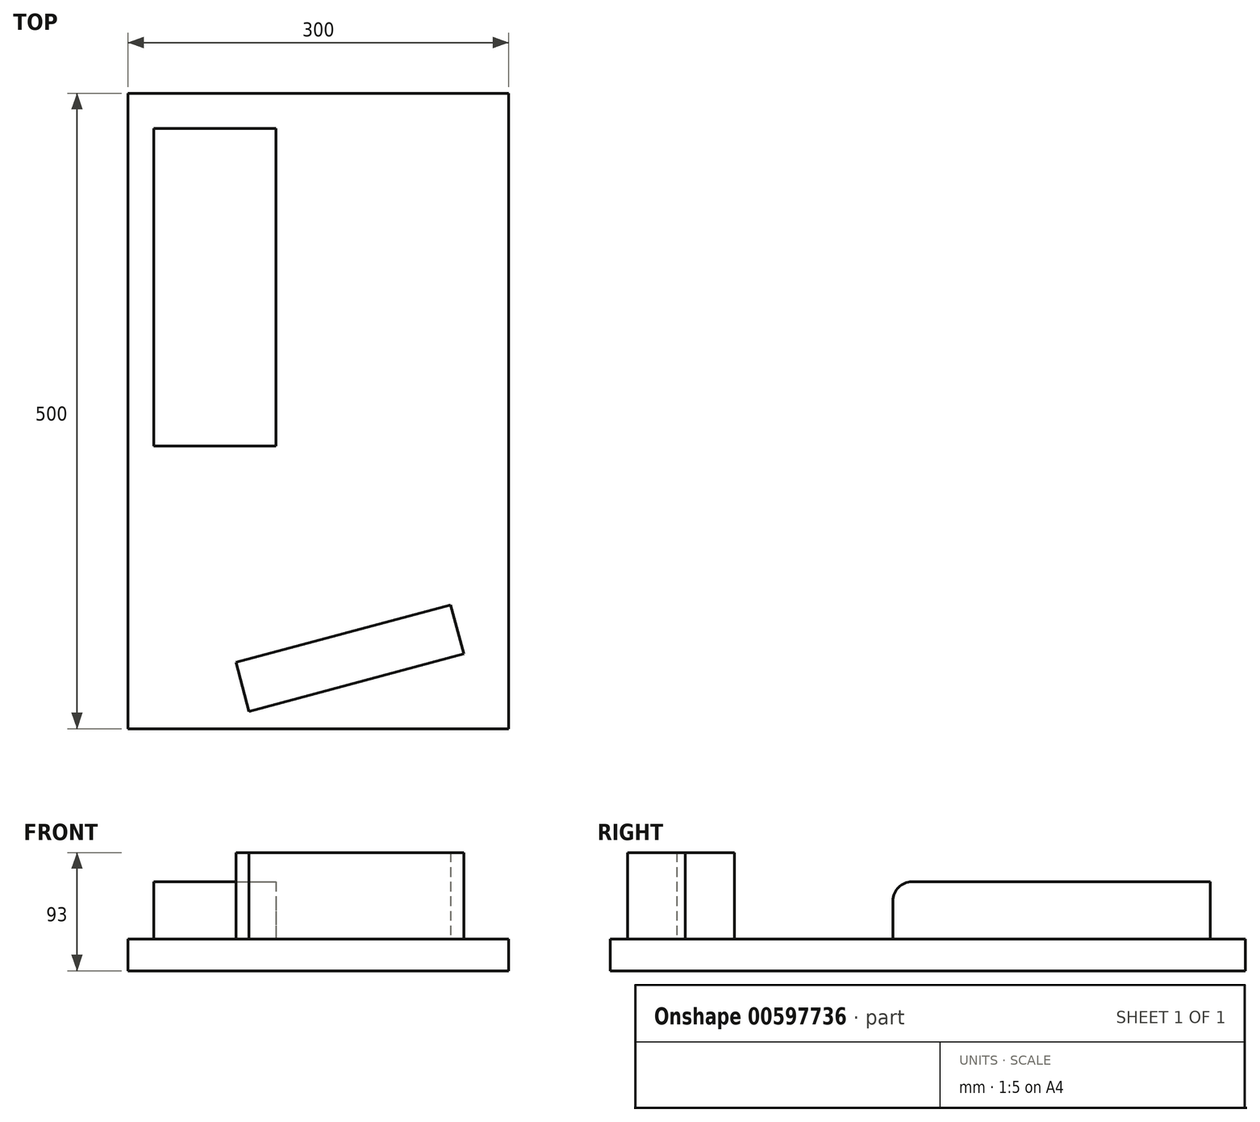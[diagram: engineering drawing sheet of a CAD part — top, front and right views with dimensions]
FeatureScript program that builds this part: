
annotation { "Feature Type Name" : "Feature", "Feature Type Description" : "" }
export const myFeature = defineFeature(function(context is Context, id is Id, definition is map)
    precondition{}
    {
        {
            var Q0;
            Q0=qCreatedBy(makeId("Top.planeOp"),FACE);
            var sketch = newSketch(context, id + "F0", { "sketchPlane" : qUnion([Q0])});
            skLineSegment(sketch, "E0.bottom", {"start": v(-250.75, 264.87) * mm, "end": v(49.25, 264.87) * mm});
            skLineSegment(sketch, "E0.top", {"start": v(-250.75, -235.13) * mm, "end": v(49.25, -235.13) * mm});
            skLineSegment(sketch, "E0.left", {"start": v(-250.75, 264.87) * mm, "end": v(-250.75, -235.13) * mm});
            skLineSegment(sketch, "E0.right", {"start": v(49.25, 264.87) * mm, "end": v(49.25, -235.13) * mm});
            skSolve(sketch);
        }
        {
            var Q0;
            Q0 = qSketchRegion(id + "F0", true);
            extrude(context, id + "F1", {"entities" : qUnion([Q0]), "depth" : 25 * mm, "offsetDistance" : 25 * mm});
        }
        {
            var Q0;
            Q0=makeQuery(id+"F1.opExtrude","CAP_FACE",FACE,{"disambiguationData":[OSD([sQuery(id+"F0.wireOp",EDGE,"E0.bottom"),sQuery(id+"F0.wireOp",EDGE,"E0.top"),sQuery(id+"F0.wireOp",EDGE,"E0.left"),sQuery(id+"F0.wireOp",EDGE,"E0.right")])],"isStart":false});
            var sketch = newSketch(context, id + "F2", { "sketchPlane" : qUnion([Q0])});
            skLineSegment(sketch, "E1.bottom", {"start": v(-230.17, 237.28) * mm, "end": v(-134.17, 237.28) * mm});
            skLineSegment(sketch, "E1.top", {"start": v(-230.17, -12.72) * mm, "end": v(-134.17, -12.72) * mm});
            skLineSegment(sketch, "E1.left", {"start": v(-230.17, 237.28) * mm, "end": v(-230.17, -12.72) * mm});
            skLineSegment(sketch, "E1.right", {"start": v(-134.17, 237.28) * mm, "end": v(-134.17, -12.72) * mm});
            skSolve(sketch);
        }
        {
            var Q0;
            Q0 = qSketchRegion(id + "F2", true);
            extrude(context, id + "F3", {"entities" : qUnion([Q0]), "operationType" : NewBodyOperationType.ADD, "depth" : 45 * mm, "offsetDistance" : 25 * mm});
        }
        {
            var Q0;
            Q0=makeQuery(id+"F1.opExtrude","CAP_FACE",FACE,{"disambiguationData":[OSD([sQuery(id+"F0.wireOp",EDGE,"E0.bottom"),sQuery(id+"F0.wireOp",EDGE,"E0.top"),sQuery(id+"F0.wireOp",EDGE,"E0.left"),sQuery(id+"F0.wireOp",EDGE,"E0.right")])],"isStart":false});
            var sketch = newSketch(context, id + "F4", { "sketchPlane" : qUnion([Q0])});
            skLineSegment(sketch, "E2", {"start": v(-165.67, -182.92) * mm, "end": v(3.37, -137.63) * mm});
            skLineSegment(sketch, "E3", {"start": v(-165.67, -182.92) * mm, "end": v(-155.32, -221.56) * mm});
            skLineSegment(sketch, "E4", {"start": v(-155.32, -221.56) * mm, "end": v(13.72, -176.27) * mm});
            skLineSegment(sketch, "E5", {"start": v(13.72, -176.27) * mm, "end": v(3.37, -137.63) * mm});
            skSolve(sketch);
        }
        {
            var Q0;
            Q0 = qSketchRegion(id + "F4", true);
            extrude(context, id + "F5", {"entities" : qUnion([Q0]), "operationType" : NewBodyOperationType.ADD, "depth" : 68 * mm, "offsetDistance" : 25 * mm});
        }
        {
            var Q0;
            Q0=makeQuery(id+"F3.opExtrude","CAP_EDGE",EDGE,{"disambiguationData":[OSD([sQuery(id+"F2.wireOp",EDGE,"E1.top")])],"isStart":false});
            fillet(context, id + "F6", {"entities" : qUnion([Q0]), "radius" : 15 * mm, "tangentPropagation" : true, "allowEdgeOverflow" : false});
        }
    });
